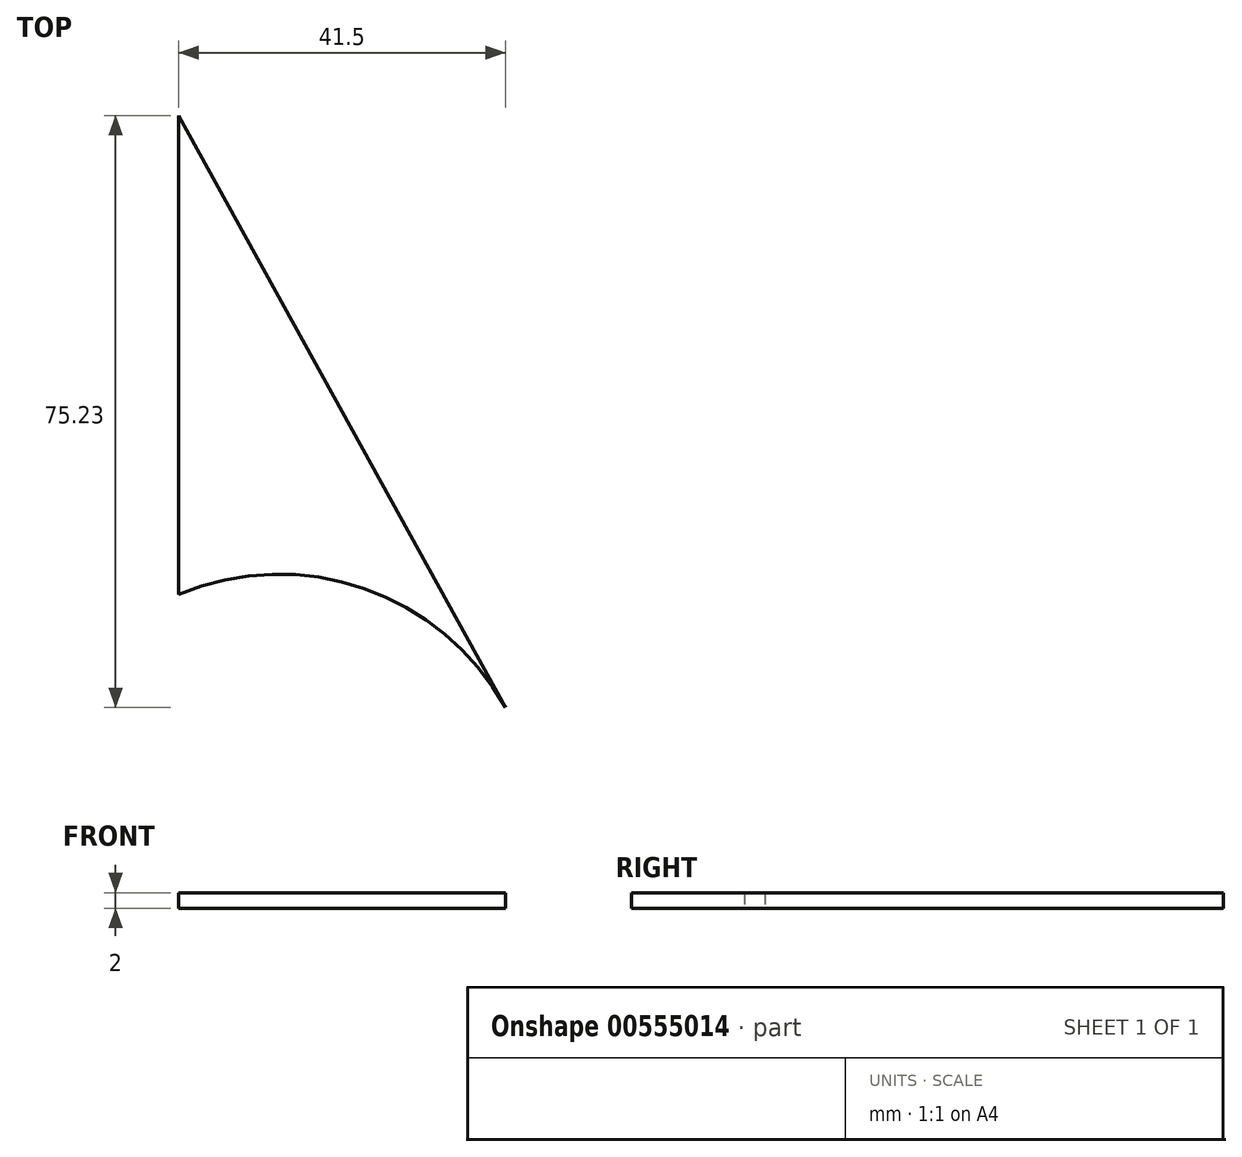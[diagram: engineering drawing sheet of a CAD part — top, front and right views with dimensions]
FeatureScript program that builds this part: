
annotation { "Feature Type Name" : "Feature", "Feature Type Description" : "" }
export const myFeature = defineFeature(function(context is Context, id is Id, definition is map)
    precondition{}
    {
        {
            var Q0;
            Q0=qCreatedBy(makeId("Top.planeOp"),FACE);
            var sketch = newSketch(context, id + "F0", { "sketchPlane" : qUnion([Q0])});
            skLineSegment(sketch, "E0", {"start": v(0, 0) * mm, "end": v(0, 60.87) * mm});
            skLineSegment(sketch, "E1", {"start": v(0, 60.87) * mm, "end": v(41.5, -14.36) * mm});
            skArc(sketch, "E2", {"start": v(41.5, -14.36) * mm, "mid": v(23.5, 0.8) * mm, "end": v(0, 0) * mm});
            skSolve(sketch);
        }
        {
            var Q0;
            Q0=makeQuery(id+"F0.imprint","IMPRINT",FACE,{"disambiguationData":[TD([[makeQuery(id+"F0.imprint","IMPRINT",EDGE,{"derivedFrom":sQuery(id+"F0.wireOp",EDGE,"E0")}),-1.0]])]});
            extrude(context, id + "F1", {"entities" : qUnion([Q0]), "depth" : 2 * mm, "offsetDistance" : 25 * mm});
        }
    });
